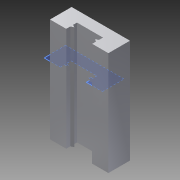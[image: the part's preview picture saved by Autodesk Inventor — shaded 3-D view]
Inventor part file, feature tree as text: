
AUTODESK INVENTOR PART (.ipt)
format: ipt  version: 2015 SP1 (Build 190203100, 203)  size: 113,152 bytes
history: native  units: mm
features: sketch x2, extrude x1, hole x1
ambient origin geometry x8: Origin, YZ Plane, XZ Plane, XY Plane, X Axis, Y Axis, Z Axis, Center Point
bodies: Solid1 (feature_tree)
feature tree (4):
  extrude  "Extrusion1"  Depth=10.0mm
  hole  "Hole1"  [1 undecoded]
  sketch  "Sketch1"  dims[d0=27.0mm d1=10.0mm]
  sketch  "Sketch2"  dims[d2=5.0mm d3=9.5mm d4=7.5mm d5=5.0mm d6=48.0mm d7=0.0mm d8=20.0mm d9=20.0mm d10=2.459mm d11=6.0mm d12=4.0mm d13=2.0mm d14=90.0deg d15=3.5mm d16=20.594885mm d17=12.0mm]
note: 1 required parameter value undecoded (feature->parameter linkage not recoverable at this tier; creation-order binding heuristic only, values carry confidence <= 0.55)
